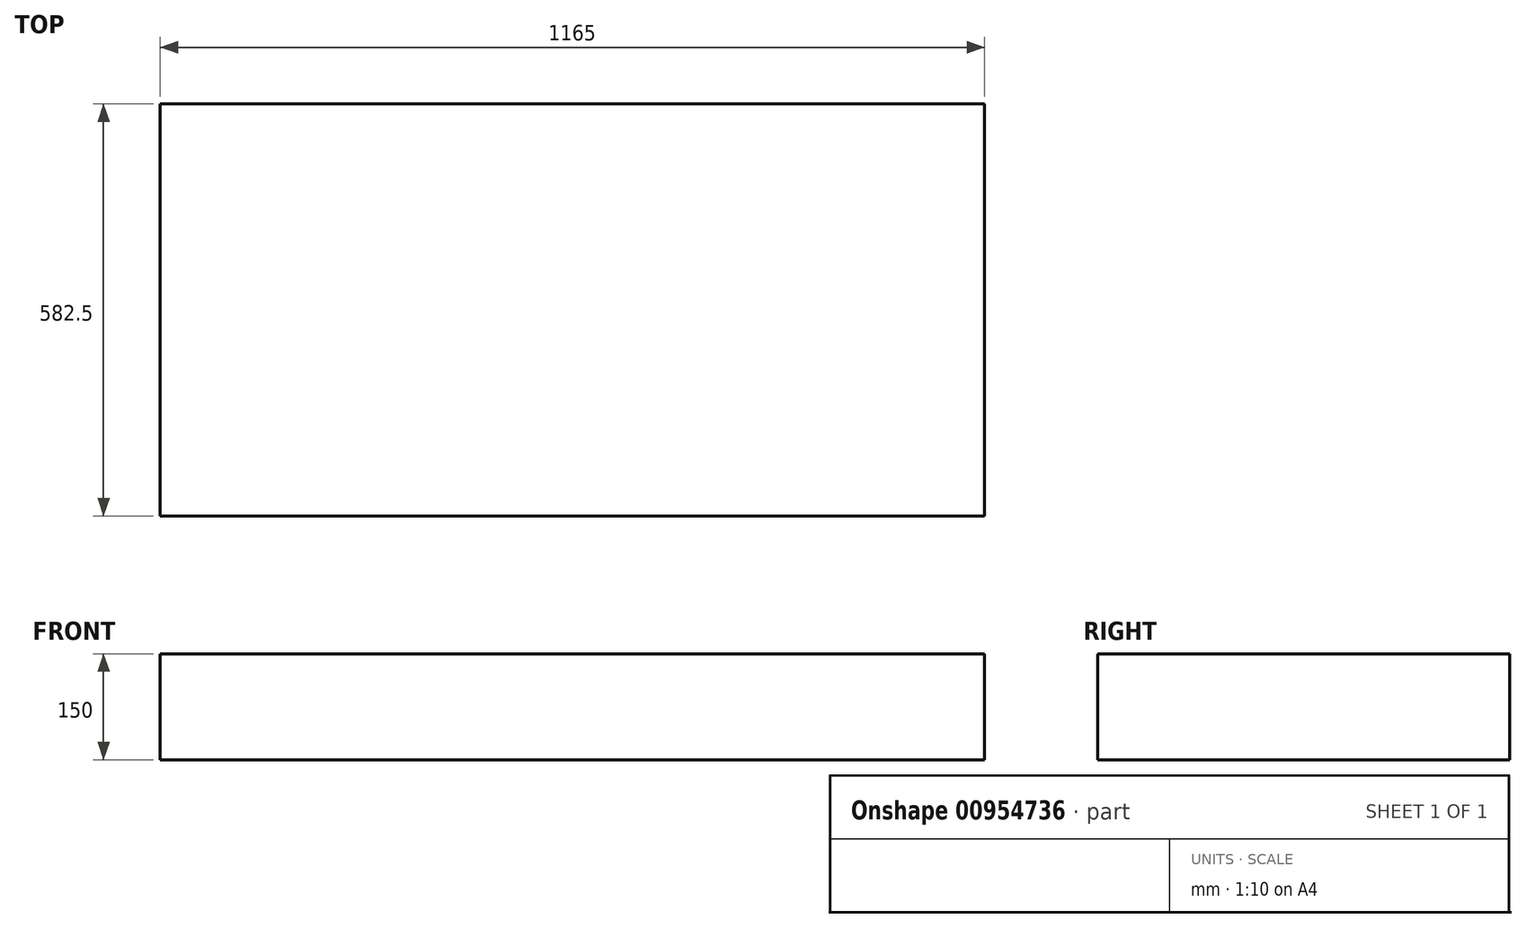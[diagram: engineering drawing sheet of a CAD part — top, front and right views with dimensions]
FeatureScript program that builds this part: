
annotation { "Feature Type Name" : "Feature", "Feature Type Description" : "" }
export const myFeature = defineFeature(function(context is Context, id is Id, definition is map)
    precondition{}
    {
        {
            var Q0;
            Q0=qCreatedBy(makeId("Top.planeOp"),FACE);
            var sketch = newSketch(context, id + "F0", { "sketchPlane" : qUnion([Q0])});
            skLineSegment(sketch, "E0.bottom", {"start": v(582.5, -291.25) * mm, "end": v(-582.5, -291.25) * mm});
            skLineSegment(sketch, "E0.top", {"start": v(582.5, 291.25) * mm, "end": v(-582.5, 291.25) * mm});
            skLineSegment(sketch, "E0.left", {"start": v(582.5, -291.25) * mm, "end": v(582.5, 291.25) * mm});
            skLineSegment(sketch, "E0.right", {"start": v(-582.5, -291.25) * mm, "end": v(-582.5, 291.25) * mm});
            skPoint(sketch, "E0.middle", {"position": v(0, 0) * mm});
            skSolve(sketch);
        }
        {
            var Q0;
            Q0=makeQuery(id+"F0.imprint","IMPRINT",FACE,{"disambiguationData":[TD([[makeQuery(id+"F0.imprint","IMPRINT",EDGE,{"derivedFrom":sQuery(id+"F0.wireOp",EDGE,"E0.bottom")}),-1.0]])]});
            extrude(context, id + "F1", {"entities" : qUnion([Q0]), "depth" : 150 * mm, "offsetDistance" : 25 * mm});
        }
    });
